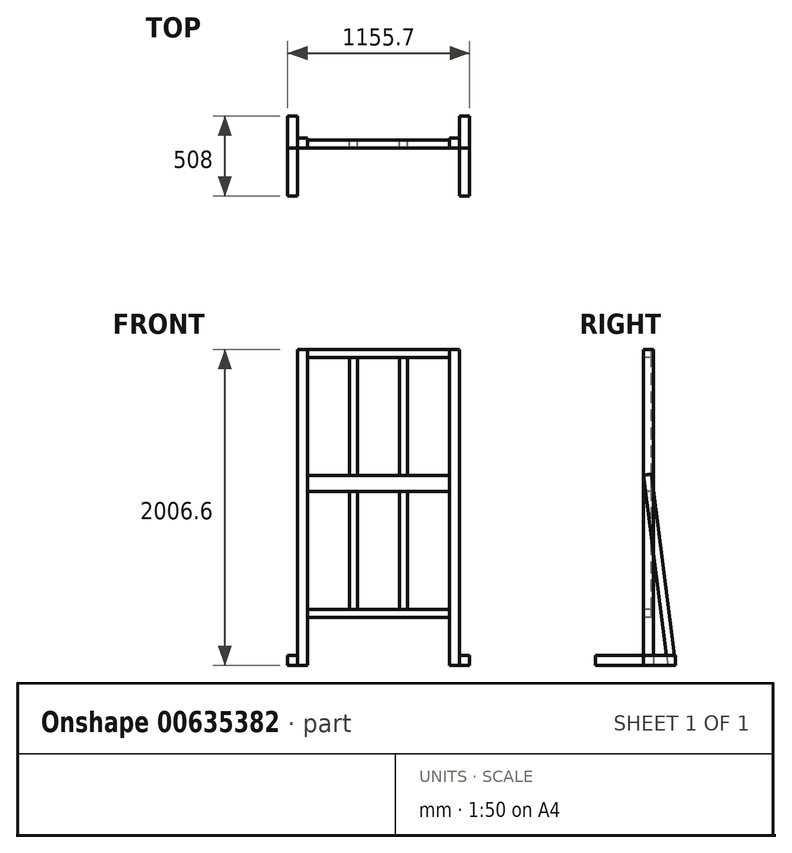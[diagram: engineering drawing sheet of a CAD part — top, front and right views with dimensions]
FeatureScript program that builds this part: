
annotation { "Feature Type Name" : "Feature", "Feature Type Description" : "" }
export const myFeature = defineFeature(function(context is Context, id is Id, definition is map)
    precondition{}
    {
        {
            var Q0;
            Q0=qCreatedBy(makeId("Top.planeOp"),FACE);
            var sketch = newSketch(context, id + "F0", { "sketchPlane" : qUnion([Q0])});
            skLineSegment(sketch, "E0.bottom", {"start": v(-514.35, 0) * mm, "end": v(-450.85, 0) * mm});
            skLineSegment(sketch, "E0.top", {"start": v(-514.35, 63.5) * mm, "end": v(-450.85, 63.5) * mm});
            skLineSegment(sketch, "E0.left", {"start": v(-514.35, 0) * mm, "end": v(-514.35, 63.5) * mm});
            skLineSegment(sketch, "E0.right", {"start": v(-450.85, 0) * mm, "end": v(-450.85, 63.5) * mm});
            skLineSegment(sketch, "E1.MirrorCS", {"start": v(450.85, 0) * mm, "end": v(450.85, 63.5) * mm});
            skLineSegment(sketch, "E2.MirrorCS", {"start": v(514.35, 0) * mm, "end": v(450.85, 0) * mm});
            skLineSegment(sketch, "E3.MirrorCS", {"start": v(514.35, 63.5) * mm, "end": v(450.85, 63.5) * mm});
            skLineSegment(sketch, "E4.MirrorCS", {"start": v(514.35, 0) * mm, "end": v(514.35, 63.5) * mm});
            skSolve(sketch);
        }
        {
            var Q0;
            Q0=makeQuery(id+"F0.imprint","IMPRINT",FACE,{"disambiguationData":[TD([[makeQuery(id+"F0.imprint","IMPRINT",EDGE,{"derivedFrom":sQuery(id+"F0.wireOp",EDGE,"E0.bottom")}),1.0]])]});
            var Q1;
            Q1=makeQuery(id+"F0.imprint","IMPRINT",FACE,{"disambiguationData":[TD([[makeQuery(id+"F0.imprint","IMPRINT",EDGE,{"derivedFrom":sQuery(id+"F0.wireOp",EDGE,"E1.MirrorCS")}),-1.0]])]});
            extrude(context, id + "F1", {"entities" : qUnion([Q0, Q1]), "depth" : 2006.6 * mm, "offsetDistance" : 25.4 * mm});
        }
        {
            var Q0;
            Q0=qCreatedBy(makeId("Front.planeOp"),FACE);
            var sketch = newSketch(context, id + "F2", { "sketchPlane" : qUnion([Q0])});
            skLineSegment(sketch, "E5.bottom", {"start": v(514.35, 0) * mm, "end": v(577.85, 0) * mm});
            skLineSegment(sketch, "E5.top", {"start": v(514.35, 63.5) * mm, "end": v(577.85, 63.5) * mm});
            skLineSegment(sketch, "E5.left", {"start": v(514.35, 0) * mm, "end": v(514.35, 63.5) * mm});
            skLineSegment(sketch, "E5.right", {"start": v(577.85, 0) * mm, "end": v(577.85, 63.5) * mm});
            skLineSegment(sketch, "E6.MirrorCS", {"start": v(-577.85, 0) * mm, "end": v(-577.85, 63.5) * mm});
            skLineSegment(sketch, "E7.MirrorCS", {"start": v(-514.35, 0) * mm, "end": v(-514.35, 63.5) * mm});
            skLineSegment(sketch, "E8.MirrorCS", {"start": v(-514.35, 0) * mm, "end": v(-577.85, 0) * mm});
            skLineSegment(sketch, "E9.MirrorCS", {"start": v(-514.35, 63.5) * mm, "end": v(-577.85, 63.5) * mm});
            skSolve(sketch);
        }
        {
            var Q0;
            Q0=makeQuery(id+"F2.imprint","IMPRINT",FACE,{"disambiguationData":[TD([[makeQuery(id+"F2.imprint","IMPRINT",EDGE,{"derivedFrom":sQuery(id+"F2.wireOp",EDGE,"E6.MirrorCS")}),-1.0]])]});
            var Q1;
            Q1=makeQuery(id+"F2.imprint","IMPRINT",FACE,{"disambiguationData":[TD([[makeQuery(id+"F2.imprint","IMPRINT",EDGE,{"derivedFrom":sQuery(id+"F2.wireOp",EDGE,"E5.bottom")}),1.0]])]});
            extrude(context, id + "F3", {"entities" : qUnion([Q0, Q1]), "depth" : 304.8 * mm, "offsetDistance" : 25.4 * mm});
        }
        {
            var Q0;
            Q0=makeQuery(id+"F3.opExtrude","CAP_FACE",FACE,{"disambiguationData":[OSD([sQuery(id+"F2.wireOp",EDGE,"E6.MirrorCS"),sQuery(id+"F2.wireOp",EDGE,"E7.MirrorCS"),sQuery(id+"F2.wireOp",EDGE,"E8.MirrorCS"),sQuery(id+"F2.wireOp",EDGE,"E9.MirrorCS")])],"isStart":true});
            var Q1;
            Q1=makeQuery(id+"F3.opExtrude","CAP_FACE",FACE,{"disambiguationData":[OSD([sQuery(id+"F2.wireOp",EDGE,"E5.bottom"),sQuery(id+"F2.wireOp",EDGE,"E5.top"),sQuery(id+"F2.wireOp",EDGE,"E5.left"),sQuery(id+"F2.wireOp",EDGE,"E5.right")])],"isStart":true});
            extrude(context, id + "F4", {"entities" : qUnion([Q0, Q1]), "depth" : 203.2 * mm, "offsetDistance" : 25.4 * mm});
        }
        {
            var Q0;
            Q0=makeQuery(id+"F1.opExtrude","SWEPT_FACE",FACE,{"disambiguationData":[OSD([sQuery(id+"F0.wireOp",EDGE,"E0.right")])]});
            var sketch = newSketch(context, id + "F5", { "sketchPlane" : qUnion([Q0])});
            skLineSegment(sketch, "E10.bottom", {"start": v(0, 2006.6) * mm, "end": v(50.8, 2006.6) * mm});
            skLineSegment(sketch, "E10.top", {"start": v(0, 1955.8) * mm, "end": v(50.8, 1955.8) * mm});
            skLineSegment(sketch, "E10.left", {"start": v(0, 2006.6) * mm, "end": v(0, 1955.8) * mm});
            skLineSegment(sketch, "E10.right", {"start": v(50.8, 2006.6) * mm, "end": v(50.8, 1955.8) * mm});
            skLineSegment(sketch, "E11.bottom", {"start": v(0, 1206.5) * mm, "end": v(50.8, 1206.5) * mm});
            skLineSegment(sketch, "E11.top", {"start": v(0, 1155.7) * mm, "end": v(50.8, 1155.7) * mm});
            skLineSegment(sketch, "E11.left", {"start": v(0, 1206.5) * mm, "end": v(0, 1155.7) * mm});
            skLineSegment(sketch, "E11.right", {"start": v(50.8, 1206.5) * mm, "end": v(50.8, 1155.7) * mm});
            skLineSegment(sketch, "E12.direction1", {"start": v(0, 1955.8) * mm, "end": v(25.4, 1955.8) * mm, "construction": true});
            skLineSegment(sketch, "E13.0.1.0", {"start": v(0, 1104.9) * mm, "end": v(50.8, 1104.9) * mm});
            skLineSegment(sketch, "E13.0.1.1", {"start": v(0, 1104.9) * mm, "end": v(25.4, 1104.9) * mm, "construction": true});
            skLineSegment(sketch, "E13.0.1.2", {"start": v(50.8, 1155.7) * mm, "end": v(50.8, 1104.9) * mm});
            skLineSegment(sketch, "E13.0.1.3", {"start": v(0, 1155.7) * mm, "end": v(0, 1104.9) * mm});
            skLineSegment(sketch, "E13.0.1.5", {"start": v(0, 304.8) * mm, "end": v(50.8, 304.8) * mm});
            skLineSegment(sketch, "E13.0.1.6", {"start": v(50.8, 355.6) * mm, "end": v(50.8, 304.8) * mm});
            skLineSegment(sketch, "E13.0.1.7", {"start": v(0, 355.6) * mm, "end": v(0, 304.8) * mm});
            skLineSegment(sketch, "E13.0.1.8", {"start": v(0, 355.6) * mm, "end": v(50.8, 355.6) * mm});
            skLineSegment(sketch, "E13.direction2", {"start": v(0, 1955.8) * mm, "end": v(0, 1104.9) * mm, "construction": true});
            skSolve(sketch);
        }
        {
            var Q0;
            Q0=makeQuery(id+"F5.imprint","IMPRINT",FACE,{"disambiguationData":[TD([[makeQuery(id+"F5.imprint","IMPRINT",EDGE,{"derivedFrom":sQuery(id+"F5.wireOp",EDGE,"E10.bottom")}),-1.0]])]});
            var Q1;
            Q1=makeQuery(id+"F5.imprint","IMPRINT",FACE,{"disambiguationData":[TD([[makeQuery(id+"F5.imprint","IMPRINT",EDGE,{"derivedFrom":sQuery(id+"F5.wireOp",EDGE,"E11.bottom")}),-1.0]])]});
            var Q2;
            Q2=makeQuery(id+"F5.imprint","IMPRINT",FACE,{"disambiguationData":[TD([[makeQuery(id+"F5.imprint","IMPRINT",EDGE,{"derivedFrom":sQuery(id+"F5.wireOp",EDGE,"E13.0.1.0")}),1.0]])]});
            var Q3;
            Q3=makeQuery(id+"F5.imprint","IMPRINT",FACE,{"disambiguationData":[TD([[makeQuery(id+"F5.imprint","IMPRINT",EDGE,{"derivedFrom":sQuery(id+"F5.wireOp",EDGE,"E13.0.1.5")}),1.0]])]});
            extrude(context, id + "F6", {"entities" : qUnion([Q0, Q1, Q2, Q3]), "endBound" : BoundingType.UP_TO_NEXT, "depth" : 25.4 * mm, "offsetDistance" : 25.4 * mm});
        }
        {
            var Q0;
            Q0=makeQuery(id+"F6.opExtrude","SWEPT_FACE",FACE,{"disambiguationData":[OSD([sQuery(id+"F5.wireOp",EDGE,"E10.top")])]});
            var sketch = newSketch(context, id + "F7", { "sketchPlane" : qUnion([Q0])});
            skLineSegment(sketch, "E14.bottom", {"start": v(-133.35, -50.8) * mm, "end": v(-184.15, -50.8) * mm});
            skLineSegment(sketch, "E14.top", {"start": v(-133.35, 0) * mm, "end": v(-184.15, 0) * mm});
            skLineSegment(sketch, "E14.left", {"start": v(-133.35, -50.8) * mm, "end": v(-133.35, 0) * mm});
            skLineSegment(sketch, "E14.right", {"start": v(-184.15, -50.8) * mm, "end": v(-184.15, 0) * mm});
            skLineSegment(sketch, "E15.bottom", {"start": v(184.15, -50.8) * mm, "end": v(133.35, -50.8) * mm});
            skLineSegment(sketch, "E15.top", {"start": v(184.15, 0) * mm, "end": v(133.35, 0) * mm});
            skLineSegment(sketch, "E15.left", {"start": v(184.15, -50.8) * mm, "end": v(184.15, 0) * mm});
            skLineSegment(sketch, "E15.right", {"start": v(133.35, -50.8) * mm, "end": v(133.35, 0) * mm});
            skSolve(sketch);
        }
        {
            var Q0;
            Q0=makeQuery(id+"F7.imprint","IMPRINT",FACE,{"disambiguationData":[TD([[makeQuery(id+"F7.imprint","IMPRINT",EDGE,{"derivedFrom":sQuery(id+"F7.wireOp",EDGE,"E14.bottom")}),-1.0]])]});
            var Q1;
            Q1=makeQuery(id+"F7.imprint","IMPRINT",FACE,{"disambiguationData":[TD([[makeQuery(id+"F7.imprint","IMPRINT",EDGE,{"derivedFrom":sQuery(id+"F7.wireOp",EDGE,"E15.bottom")}),-1.0]])]});
            extrude(context, id + "F8", {"entities" : qUnion([Q0, Q1]), "endBound" : BoundingType.UP_TO_NEXT, "depth" : 25.4 * mm, "offsetDistance" : 25.4 * mm});
        }
        {
            var Q0;
            Q0=makeQuery(id+"F6.opExtrude","SWEPT_FACE",FACE,{"disambiguationData":[OSD([sQuery(id+"F5.wireOp",EDGE,"E13.0.1.0")])]});
            var sketch = newSketch(context, id + "F9", { "sketchPlane" : qUnion([Q0])});
            skLineSegment(sketch, "E16.bottom", {"start": v(184.15, -50.8) * mm, "end": v(133.35, -50.8) * mm});
            skLineSegment(sketch, "E16.top", {"start": v(184.15, 0) * mm, "end": v(133.35, 0) * mm});
            skLineSegment(sketch, "E16.left", {"start": v(184.15, -50.8) * mm, "end": v(184.15, 0) * mm});
            skLineSegment(sketch, "E16.right", {"start": v(133.35, -50.8) * mm, "end": v(133.35, 0) * mm});
            skLineSegment(sketch, "E17.bottom", {"start": v(-133.35, -50.8) * mm, "end": v(-184.15, -50.8) * mm});
            skLineSegment(sketch, "E17.top", {"start": v(-133.35, 0) * mm, "end": v(-184.15, 0) * mm});
            skLineSegment(sketch, "E17.left", {"start": v(-133.35, -50.8) * mm, "end": v(-133.35, 0) * mm});
            skLineSegment(sketch, "E17.right", {"start": v(-184.15, -50.8) * mm, "end": v(-184.15, 0) * mm});
            skSolve(sketch);
        }
        {
            var Q0;
            Q0=makeQuery(id+"F9.imprint","IMPRINT",FACE,{"disambiguationData":[TD([[makeQuery(id+"F9.imprint","IMPRINT",EDGE,{"derivedFrom":sQuery(id+"F9.wireOp",EDGE,"E16.bottom")}),-1.0]])]});
            var Q1;
            Q1=makeQuery(id+"F9.imprint","IMPRINT",FACE,{"disambiguationData":[TD([[makeQuery(id+"F9.imprint","IMPRINT",EDGE,{"derivedFrom":sQuery(id+"F9.wireOp",EDGE,"E17.bottom")}),-1.0]])]});
            extrude(context, id + "F10", {"entities" : qUnion([Q0, Q1]), "endBound" : BoundingType.UP_TO_NEXT, "depth" : 25.4 * mm, "offsetDistance" : 25.4 * mm});
        }
        {
            var Q0;
            Q0=makeQuery(id+"F1.opExtrude","SWEPT_FACE",FACE,{"disambiguationData":[OSD([sQuery(id+"F0.wireOp",EDGE,"E0.left")])]});
            var sketch = newSketch(context, id + "F11", { "sketchPlane" : qUnion([Q0])});
            skLineSegment(sketch, "E18", {"start": v(-50.4, 1215.95) * mm, "end": v(0, 1209.59) * mm});
            skLineSegment(sketch, "E19", {"start": v(0, 1209.59) * mm, "end": v(-152.8, 0) * mm});
            skLineSegment(sketch, "E20", {"start": v(-152.8, 0) * mm, "end": v(-203.2, 6.37) * mm});
            skLineSegment(sketch, "E21", {"start": v(-203.2, 6.37) * mm, "end": v(-50.4, 1215.95) * mm});
            skSolve(sketch);
        }
        {
            var Q0;
            {var subQ0=sQuery(id+"F11.wireOp",EDGE,"E20");Q0=makeQuery(id+"F11.imprint","IMPRINT",FACE,{"disambiguationData":[TD([[makeQuery(id+"F11.imprint","IMPRINT",EDGE,{"derivedFrom":subQ0}),-1.0]])]});}
            var Q1;
            {var subQ0=sQuery(id+"F11.wireOp",EDGE,"E18");Q1=makeQuery(id+"F11.imprint","IMPRINT",FACE,{"disambiguationData":[TD([[makeQuery(id+"F11.imprint","IMPRINT",EDGE,{"derivedFrom":subQ0}),-1.0]])]});}
            extrude(context, id + "F12", {"entities" : qUnion([Q0, Q1]), "depth" : 1 / 203.2 * mm, "offsetDistance" : 25.4 * mm});
        }
        {
            var Q0;
            Q0=makeQuery(id+"F12.opExtrude","SWEPT_BODY",BODY,{"disambiguationData":[OSD([sQuery(id+"F11.wireOp",EDGE,"E18"),sQuery(id+"F11.wireOp",EDGE,"E19"),sQuery(id+"F11.wireOp",EDGE,"E20"),sQuery(id+"F11.wireOp",EDGE,"E21")])]});
            var Q1;
            Q1=qCreatedBy(makeId("Right.planeOp"),FACE);
            mirror(context, id + "F13", {"entities" : qUnion([Q0]), "mirrorPlane" : qUnion([Q1])});
        }
    });
